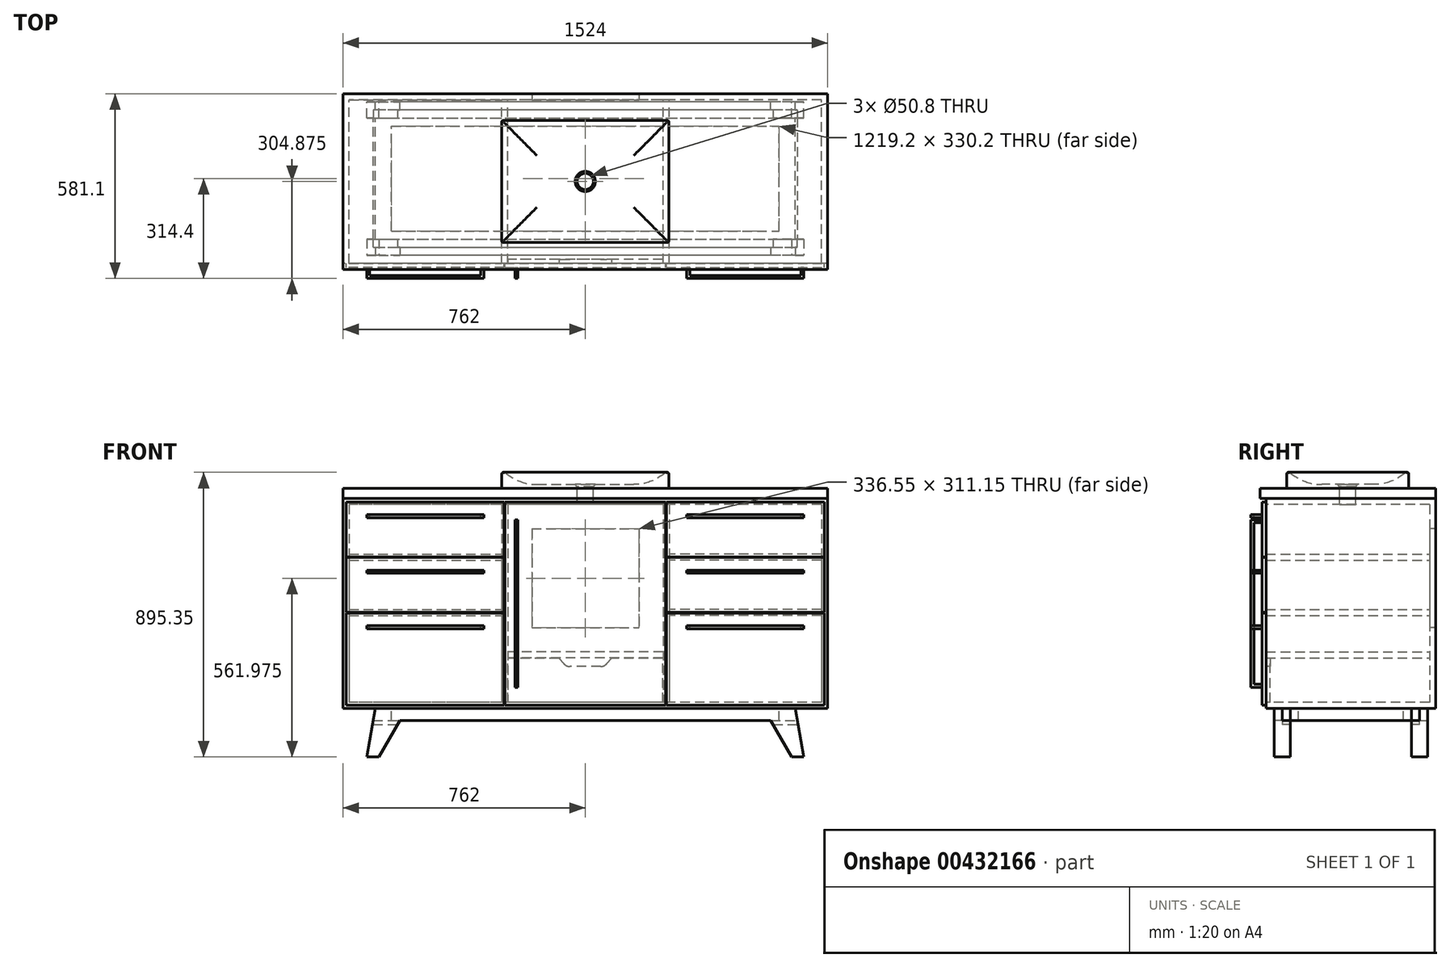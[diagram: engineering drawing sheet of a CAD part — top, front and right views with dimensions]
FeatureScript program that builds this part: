
annotation { "Feature Type Name" : "Feature", "Feature Type Description" : "" }
export const myFeature = defineFeature(function(context is Context, id is Id, definition is map)
    precondition{}
    {
        {
            var Q0;
            Q0=qCreatedBy(makeId("Front.planeOp"),FACE);
            var sketch = newSketch(context, id + "F0", { "sketchPlane" : qUnion([Q0])});
            skLineSegment(sketch, "E0.bottom", {"start": v(762, 330.2) * mm, "end": v(-762, 330.2) * mm});
            skLineSegment(sketch, "E0.top", {"start": v(762, -330.2) * mm, "end": v(-762, -330.2) * mm});
            skLineSegment(sketch, "E0.left", {"start": v(762, 330.2) * mm, "end": v(762, -330.2) * mm});
            skLineSegment(sketch, "E0.right", {"start": v(-762, 330.2) * mm, "end": v(-762, -330.2) * mm});
            skPoint(sketch, "E0.middle", {"position": v(0, 0) * mm});
            skSolve(sketch);
        }
        {
            var Q0;
            Q0=makeQuery(id+"F0.imprint","IMPRINT",FACE,{"disambiguationData":[TD([[makeQuery(id+"F0.imprint","IMPRINT",EDGE,{"derivedFrom":sQuery(id+"F0.wireOp",EDGE,"E0.bottom")}),1.0]])]});
            extrude(context, id + "F1", {"entities" : qUnion([Q0]), "oppositeDirection" : true, "depth" : 533.4 * mm});
        }
        {
            var Q0;
            Q0=makeQuery(id+"F1.opExtrude","CAP_FACE",FACE,{"disambiguationData":[OSD([sQuery(id+"F0.wireOp",EDGE,"E0.bottom"),sQuery(id+"F0.wireOp",EDGE,"E0.top"),sQuery(id+"F0.wireOp",EDGE,"E0.left"),sQuery(id+"F0.wireOp",EDGE,"E0.right")])],"isStart":true});
            var sketch = newSketch(context, id + "F2", { "sketchPlane" : qUnion([Q0])});
            skLineSegment(sketch, "E1.bottom", {"start": v(742.95, 311.15) * mm, "end": v(-742.95, 311.15) * mm});
            skLineSegment(sketch, "E1.top", {"start": v(742.95, -311.15) * mm, "end": v(-742.95, -311.15) * mm});
            skLineSegment(sketch, "E1.left", {"start": v(742.95, 311.15) * mm, "end": v(742.95, -311.15) * mm});
            skLineSegment(sketch, "E1.right", {"start": v(-742.95, 311.15) * mm, "end": v(-742.95, -311.15) * mm});
            skPoint(sketch, "E1.middle", {"position": v(0, 0) * mm});
            skSolve(sketch);
        }
        {
            var Q0;
            Q0=makeQuery(id+"F2.imprint","IMPRINT",FACE,{"disambiguationData":[TD([[makeQuery(id+"F2.imprint","IMPRINT",EDGE,{"derivedFrom":sQuery(id+"F2.wireOp",EDGE,"E1.bottom")}),1.0]])]});
            extrude(context, id + "F3", {"entities" : qUnion([Q0]), "operationType" : NewBodyOperationType.REMOVE, "oppositeDirection" : true, "depth" : 514.35 * mm});
        }
        {
            var Q0;
            Q0=makeQuery(id+"F3.boolean.opBoolean","COPY",FACE,{"derivedFrom":makeQuery(id+"F3.opExtrude","CAP_FACE",FACE,{"disambiguationData":[OSD([sQuery(id+"F2.wireOp",EDGE,"E1.bottom"),sQuery(id+"F2.wireOp",EDGE,"E1.top"),sQuery(id+"F2.wireOp",EDGE,"E1.left"),sQuery(id+"F2.wireOp",EDGE,"E1.right")])],"isStart":false})});
            var sketch = newSketch(context, id + "F4", { "sketchPlane" : qUnion([Q0])});
            skLineSegment(sketch, "E2.bottom", {"start": v(-263.52, 311.15) * mm, "end": v(-244.47, 311.15) * mm});
            skLineSegment(sketch, "E2.top", {"start": v(-263.52, -311.15) * mm, "end": v(-244.47, -311.15) * mm});
            skLineSegment(sketch, "E2.left", {"start": v(-263.53, 311.15) * mm, "end": v(-263.53, -311.15) * mm});
            skLineSegment(sketch, "E2.right", {"start": v(-244.47, 311.15) * mm, "end": v(-244.47, -311.15) * mm});
            skPoint(sketch, "E2.middle", {"position": v(-254, 0) * mm});
            skLineSegment(sketch, "E3.bottom", {"start": v(244.47, 311.15) * mm, "end": v(263.52, 311.15) * mm});
            skLineSegment(sketch, "E3.top", {"start": v(244.47, -311.15) * mm, "end": v(263.52, -311.15) * mm});
            skLineSegment(sketch, "E3.left", {"start": v(244.47, 311.15) * mm, "end": v(244.47, -311.15) * mm});
            skLineSegment(sketch, "E3.right", {"start": v(263.53, 311.15) * mm, "end": v(263.53, -311.15) * mm});
            skPoint(sketch, "E3.middle", {"position": v(254, 0) * mm});
            skLineSegment(sketch, "E4", {"start": v(-742.95, 0) * mm, "end": v(742.95, 0) * mm, "construction": true});
            skSolve(sketch);
        }
        {
            var Q0;
            Q0=makeQuery(id+"F4.imprint","IMPRINT",FACE,{"disambiguationData":[TD([[makeQuery(id+"F4.imprint","IMPRINT",EDGE,{"derivedFrom":sQuery(id+"F4.wireOp",EDGE,"E2.bottom")}),1.0]])]});
            var Q1;
            Q1=makeQuery(id+"F4.imprint","IMPRINT",FACE,{"disambiguationData":[TD([[makeQuery(id+"F4.imprint","IMPRINT",EDGE,{"derivedFrom":sQuery(id+"F4.wireOp",EDGE,"E3.bottom")}),1.0]])]});
            var Q2;
            Q2=makeQuery(id+"F1.opExtrude","CAP_FACE",FACE,{"disambiguationData":[OSD([sQuery(id+"F0.wireOp",EDGE,"E0.bottom"),sQuery(id+"F0.wireOp",EDGE,"E0.top"),sQuery(id+"F0.wireOp",EDGE,"E0.left"),sQuery(id+"F0.wireOp",EDGE,"E0.right")])],"isStart":true});
            extrude(context, id + "F5", {"entities" : qUnion([Q0, Q1]), "endBound" : BoundingType.UP_TO_SURFACE, "endBoundEntityFace" : qUnion([Q2]), "depth" : ((2 * 12) - .75 - .75) * mm});
        }
        {
            var Q0;
            Q0=makeQuery(id+"F3.boolean.opBoolean","COPY",FACE,{"derivedFrom":makeQuery(id+"F3.opExtrude","CAP_FACE",FACE,{"disambiguationData":[OSD([sQuery(id+"F2.wireOp",EDGE,"E1.bottom"),sQuery(id+"F2.wireOp",EDGE,"E1.top"),sQuery(id+"F2.wireOp",EDGE,"E1.left"),sQuery(id+"F2.wireOp",EDGE,"E1.right")])],"isStart":false})});
            var sketch = newSketch(context, id + "F6", { "sketchPlane" : qUnion([Q0])});
            skLineSegment(sketch, "E5", {"start": v(-742.95, 311.15) * mm, "end": v(-263.53, 311.15) * mm, "construction": true});
            skLineSegment(sketch, "E6.bottom", {"start": v(-742.95, 155.58) * mm, "end": v(-263.53, 155.58) * mm});
            skLineSegment(sketch, "E6.top", {"start": v(-742.95, 136.53) * mm, "end": v(-263.53, 136.53) * mm});
            skLineSegment(sketch, "E6.left", {"start": v(-742.95, 155.58) * mm, "end": v(-742.95, 136.53) * mm});
            skLineSegment(sketch, "E6.right", {"start": v(-263.53, 155.58) * mm, "end": v(-263.53, 136.53) * mm});
            skPoint(sketch, "E6.middle", {"position": v(-503.24, 146.05) * mm});
            skPoint(sketch, "E6.middle.positionSnap0", {"position": v(-503.24, 311.15) * mm});
            skPoint(sketch, "E6.centerSnap0", {"position": v(-503.24, 311.15) * mm});
            skLineSegment(sketch, "E7.bottom", {"start": v(-742.95, -19.05) * mm, "end": v(-263.53, -19.05) * mm});
            skLineSegment(sketch, "E7.top", {"start": v(-742.95, -38.1) * mm, "end": v(-263.53, -38.1) * mm});
            skLineSegment(sketch, "E7.left", {"start": v(-742.95, -19.05) * mm, "end": v(-742.95, -38.1) * mm});
            skLineSegment(sketch, "E7.right", {"start": v(-263.53, -19.05) * mm, "end": v(-263.53, -38.1) * mm});
            skPoint(sketch, "E7.middle", {"position": v(-503.24, -28.57) * mm});
            skLineSegment(sketch, "E8", {"start": v(0, 311.15) * mm, "end": v(0, -311.15) * mm, "construction": true});
            skLineSegment(sketch, "E9.MirrorCS", {"start": v(263.53, -19.05) * mm, "end": v(263.53, -38.1) * mm});
            skLineSegment(sketch, "E10.MirrorCS", {"start": v(742.95, -19.05) * mm, "end": v(742.95, -38.1) * mm});
            skLineSegment(sketch, "E11.MirrorCS", {"start": v(742.95, 155.58) * mm, "end": v(742.95, 136.53) * mm});
            skLineSegment(sketch, "E12.MirrorCS", {"start": v(263.53, 155.58) * mm, "end": v(263.53, 136.53) * mm});
            skPoint(sketch, "E13.MirrorP", {"position": v(503.24, 311.15) * mm});
            skLineSegment(sketch, "E14.MirrorCS", {"start": v(742.95, 155.58) * mm, "end": v(263.53, 155.57) * mm});
            skPoint(sketch, "E15.MirrorP", {"position": v(503.24, -28.57) * mm});
            skLineSegment(sketch, "E16.MirrorCS", {"start": v(742.95, -38.1) * mm, "end": v(263.53, -38.1) * mm});
            skLineSegment(sketch, "E17.MirrorCS", {"start": v(742.95, -19.05) * mm, "end": v(263.53, -19.05) * mm});
            skLineSegment(sketch, "E18.MirrorCS", {"start": v(742.95, 136.53) * mm, "end": v(263.53, 136.53) * mm});
            skLineSegment(sketch, "E19.MirrorCS", {"start": v(742.95, 311.15) * mm, "end": v(263.53, 311.15) * mm, "construction": true});
            skPoint(sketch, "E20.MirrorP", {"position": v(503.24, 146.05) * mm});
            skPoint(sketch, "E21.cornerSnap0", {"position": v(-503.24, -19.05) * mm});
            skPoint(sketch, "E22.middle", {"position": v(0, 146.05) * mm});
            skLineSegment(sketch, "E23.bottom", {"start": v(244.47, -152.4) * mm, "end": v(-244.47, -152.4) * mm});
            skLineSegment(sketch, "E23.top", {"start": v(244.47, -171.45) * mm, "end": v(-244.47, -171.45) * mm});
            skLineSegment(sketch, "E23.left", {"start": v(244.47, -152.4) * mm, "end": v(244.47, -171.45) * mm});
            skLineSegment(sketch, "E23.right", {"start": v(-244.47, -152.4) * mm, "end": v(-244.47, -171.45) * mm});
            skPoint(sketch, "E23.middle", {"position": v(0, -161.93) * mm});
            skSolve(sketch);
        }
        {
            var Q0;
            Q0=makeQuery(id+"F6.imprint","IMPRINT",FACE,{"disambiguationData":[TD([[makeQuery(id+"F6.imprint","IMPRINT",EDGE,{"derivedFrom":sQuery(id+"F6.wireOp",EDGE,"E6.bottom")}),-1.0]])]});
            var Q1;
            Q1=makeQuery(id+"F6.imprint","IMPRINT",FACE,{"disambiguationData":[TD([[makeQuery(id+"F6.imprint","IMPRINT",EDGE,{"derivedFrom":sQuery(id+"F6.wireOp",EDGE,"E7.bottom")}),-1.0]])]});
            var Q2;
            Q2=makeQuery(id+"F6.imprint","IMPRINT",FACE,{"disambiguationData":[TD([[makeQuery(id+"F6.imprint","IMPRINT",EDGE,{"derivedFrom":sQuery(id+"F6.wireOp",EDGE,"E11.MirrorCS")}),-1.0]])]});
            var Q3;
            Q3=makeQuery(id+"F6.imprint","IMPRINT",FACE,{"disambiguationData":[TD([[makeQuery(id+"F6.imprint","IMPRINT",EDGE,{"derivedFrom":sQuery(id+"F6.wireOp",EDGE,"E9.MirrorCS")}),1.0]])]});
            var Q4;
            Q4=makeQuery(id+"F1.opExtrude","CAP_FACE",FACE,{"disambiguationData":[OSD([sQuery(id+"F0.wireOp",EDGE,"E0.bottom"),sQuery(id+"F0.wireOp",EDGE,"E0.top"),sQuery(id+"F0.wireOp",EDGE,"E0.left"),sQuery(id+"F0.wireOp",EDGE,"E0.right")])],"isStart":true});
            extrude(context, id + "F7", {"entities" : qUnion([Q0, Q1, Q2, Q3]), "endBound" : BoundingType.UP_TO_SURFACE, "endBoundEntityFace" : qUnion([Q4]), "depth" : 571.5 * mm});
        }
        {
            var Q0;
            Q0=makeQuery(id+"F7.opExtrude","CAP_FACE",FACE,{"disambiguationData":[OSD([sQuery(id+"F6.wireOp",EDGE,"E7.bottom"),sQuery(id+"F6.wireOp",EDGE,"E7.top"),sQuery(id+"F6.wireOp",EDGE,"E7.left"),sQuery(id+"F6.wireOp",EDGE,"E7.right")])],"isStart":false});
            var sketch = newSketch(context, id + "F8", { "sketchPlane" : qUnion([Q0])});
            skLineSegment(sketch, "E24.bottom", {"start": v(-742.95, -38.1) * mm, "end": v(-263.53, -38.1) * mm, "construction": true});
            skLineSegment(sketch, "E24.top", {"start": v(-742.95, -311.15) * mm, "end": v(-263.53, -311.15) * mm, "construction": true});
            skLineSegment(sketch, "E24.left", {"start": v(-742.95, -38.1) * mm, "end": v(-742.95, -311.15) * mm, "construction": true});
            skLineSegment(sketch, "E24.right", {"start": v(-263.52, -38.1) * mm, "end": v(-263.52, -311.15) * mm, "construction": true});
            skLineSegment(sketch, "E25.bottom", {"start": v(-742.95, -19.05) * mm, "end": v(-263.53, -19.05) * mm, "construction": true});
            skLineSegment(sketch, "E25.top", {"start": v(-742.95, 136.53) * mm, "end": v(-263.53, 136.53) * mm, "construction": true});
            skLineSegment(sketch, "E25.left", {"start": v(-742.95, -19.05) * mm, "end": v(-742.95, 136.53) * mm, "construction": true});
            skLineSegment(sketch, "E25.right", {"start": v(-263.53, -19.05) * mm, "end": v(-263.53, 136.53) * mm, "construction": true});
            skLineSegment(sketch, "E26.bottom", {"start": v(-742.95, 311.15) * mm, "end": v(-263.52, 311.15) * mm, "construction": true});
            skLineSegment(sketch, "E26.top", {"start": v(-742.95, 155.58) * mm, "end": v(-263.53, 155.58) * mm, "construction": true});
            skLineSegment(sketch, "E26.left", {"start": v(-742.95, 311.15) * mm, "end": v(-742.95, 155.58) * mm, "construction": true});
            skLineSegment(sketch, "E26.right", {"start": v(-263.52, 311.15) * mm, "end": v(-263.52, 155.58) * mm, "construction": true});
            skLineSegment(sketch, "E27", {"start": v(0, 311.15) * mm, "end": v(0, -311.15) * mm, "construction": true});
            skLineSegment(sketch, "E28.bottom", {"start": v(-254.8, 146.84) * mm, "end": v(-751.68, 146.84) * mm});
            skLineSegment(sketch, "E28.top", {"start": v(-254.8, 319.88) * mm, "end": v(-751.68, 319.88) * mm});
            skLineSegment(sketch, "E28.left", {"start": v(-254.8, 146.84) * mm, "end": v(-254.8, 319.88) * mm});
            skLineSegment(sketch, "E28.right", {"start": v(-751.68, 146.84) * mm, "end": v(-751.68, 319.88) * mm});
            skPoint(sketch, "E28.middle", {"position": v(-503.24, 233.36) * mm});
            skPoint(sketch, "E28.middle.positionSnap0", {"position": v(-503.24, 311.15) * mm});
            skPoint(sketch, "E28.middle.positionSnap1", {"position": v(-742.95, 233.36) * mm});
            skPoint(sketch, "E28.centerSnap0", {"position": v(-503.24, 311.15) * mm});
            skPoint(sketch, "E28.centerSnap1", {"position": v(-742.95, 233.36) * mm});
            skPoint(sketch, "E29.middle.positionSnap0", {"position": v(-503.24, 136.52) * mm});
            skPoint(sketch, "E29.middle.positionSnap1", {"position": v(-742.95, 58.74) * mm});
            skPoint(sketch, "E29.centerSnap0", {"position": v(-503.24, 136.52) * mm});
            skPoint(sketch, "E29.centerSnap1", {"position": v(-742.95, 58.74) * mm});
            skLineSegment(sketch, "E30.bottom", {"start": v(-254.8, -29.37) * mm, "end": v(-751.68, -29.37) * mm});
            skLineSegment(sketch, "E30.top", {"start": v(-254.8, -319.88) * mm, "end": v(-751.68, -319.88) * mm});
            skLineSegment(sketch, "E30.left", {"start": v(-254.8, -29.37) * mm, "end": v(-254.8, -319.88) * mm});
            skLineSegment(sketch, "E30.right", {"start": v(-751.68, -29.37) * mm, "end": v(-751.68, -319.88) * mm});
            skPoint(sketch, "E30.middle", {"position": v(-503.24, -174.63) * mm});
            skPoint(sketch, "E30.middle.positionSnap0", {"position": v(-742.95, -174.63) * mm});
            skPoint(sketch, "E30.middle.positionSnap1", {"position": v(-503.24, -38.1) * mm});
            skPoint(sketch, "E30.centerSnap0", {"position": v(-742.95, -174.63) * mm});
            skPoint(sketch, "E30.centerSnap1", {"position": v(-503.24, -38.1) * mm});
            skLineSegment(sketch, "E31.bottom", {"start": v(-751.68, 145.26) * mm, "end": v(-254.8, 145.26) * mm});
            skLineSegment(sketch, "E31.top", {"start": v(-751.68, -27.78) * mm, "end": v(-254.8, -27.78) * mm});
            skLineSegment(sketch, "E31.left", {"start": v(-751.68, 145.26) * mm, "end": v(-751.68, -27.78) * mm});
            skLineSegment(sketch, "E31.right", {"start": v(-254.8, 145.26) * mm, "end": v(-254.8, -27.78) * mm});
            skPoint(sketch, "E31.middle", {"position": v(-503.24, 58.74) * mm});
            skLineSegment(sketch, "E32.MirrorCS", {"start": v(751.68, 146.84) * mm, "end": v(751.68, 319.88) * mm});
            skLineSegment(sketch, "E33.MirrorCS", {"start": v(751.68, 145.26) * mm, "end": v(751.68, -27.78) * mm});
            skLineSegment(sketch, "E34.MirrorCS", {"start": v(254.8, -319.88) * mm, "end": v(751.68, -319.88) * mm});
            skPoint(sketch, "E35.MirrorP", {"position": v(742.95, -174.62) * mm});
            skLineSegment(sketch, "E36.MirrorCS", {"start": v(751.68, -27.78) * mm, "end": v(254.8, -27.78) * mm});
            skLineSegment(sketch, "E37.MirrorCS", {"start": v(254.8, 146.84) * mm, "end": v(751.68, 146.84) * mm});
            skLineSegment(sketch, "E38.MirrorCS", {"start": v(254.8, -29.37) * mm, "end": v(254.8, -319.88) * mm});
            skPoint(sketch, "E39.MirrorP", {"position": v(503.24, 311.15) * mm});
            skPoint(sketch, "E40.MirrorP", {"position": v(503.24, -38.1) * mm});
            skLineSegment(sketch, "E41.MirrorCS", {"start": v(254.8, 319.88) * mm, "end": v(751.68, 319.88) * mm});
            skLineSegment(sketch, "E42.MirrorCS", {"start": v(751.68, 145.26) * mm, "end": v(254.8, 145.26) * mm});
            skPoint(sketch, "E43.MirrorP", {"position": v(742.95, 233.36) * mm});
            skLineSegment(sketch, "E44.MirrorCS", {"start": v(254.8, 146.84) * mm, "end": v(254.8, 319.88) * mm});
            skLineSegment(sketch, "E45.MirrorCS", {"start": v(751.68, -29.37) * mm, "end": v(751.68, -319.88) * mm});
            skPoint(sketch, "E46.MirrorP", {"position": v(503.24, 136.53) * mm});
            skLineSegment(sketch, "E47.MirrorCS", {"start": v(254.8, 145.26) * mm, "end": v(254.8, -27.78) * mm});
            skPoint(sketch, "E48.MirrorP", {"position": v(742.95, 58.74) * mm});
            skPoint(sketch, "E49.MirrorP", {"position": v(503.24, 233.36) * mm});
            skLineSegment(sketch, "E50.MirrorCS", {"start": v(742.95, -311.15) * mm, "end": v(263.53, -311.15) * mm, "construction": true});
            skLineSegment(sketch, "E51.MirrorCS", {"start": v(742.95, -19.05) * mm, "end": v(742.95, 136.53) * mm, "construction": true});
            skLineSegment(sketch, "E52.MirrorCS", {"start": v(742.95, -38.1) * mm, "end": v(742.95, -311.15) * mm, "construction": true});
            skPoint(sketch, "E53.MirrorP", {"position": v(503.24, 58.74) * mm});
            skLineSegment(sketch, "E54.MirrorCS", {"start": v(263.52, -38.1) * mm, "end": v(263.52, -311.15) * mm, "construction": true});
            skLineSegment(sketch, "E55.MirrorCS", {"start": v(742.95, -19.05) * mm, "end": v(263.53, -19.05) * mm, "construction": true});
            skLineSegment(sketch, "E56.MirrorCS", {"start": v(263.52, 311.15) * mm, "end": v(263.52, 155.58) * mm, "construction": true});
            skLineSegment(sketch, "E57.MirrorCS", {"start": v(742.95, 311.15) * mm, "end": v(742.95, 155.58) * mm, "construction": true});
            skLineSegment(sketch, "E58.MirrorCS", {"start": v(742.95, -38.1) * mm, "end": v(263.53, -38.1) * mm, "construction": true});
            skLineSegment(sketch, "E59.MirrorCS", {"start": v(742.95, 155.58) * mm, "end": v(263.52, 155.58) * mm, "construction": true});
            skLineSegment(sketch, "E60.MirrorCS", {"start": v(742.95, 136.53) * mm, "end": v(263.53, 136.53) * mm, "construction": true});
            skPoint(sketch, "E61.MirrorP", {"position": v(503.24, -174.62) * mm});
            skLineSegment(sketch, "E62.MirrorCS", {"start": v(263.53, -19.05) * mm, "end": v(263.53, 136.53) * mm, "construction": true});
            skLineSegment(sketch, "E63.MirrorCS", {"start": v(254.8, -29.37) * mm, "end": v(751.68, -29.37) * mm});
            skLineSegment(sketch, "E64.MirrorCS", {"start": v(742.95, 311.15) * mm, "end": v(263.52, 311.15) * mm, "construction": true});
            skSolve(sketch);
        }
        {
            var Q0;
            Q0=makeQuery(id+"F8.imprint","IMPRINT",FACE,{"disambiguationData":[TD([[makeQuery(id+"F8.imprint","IMPRINT",EDGE,{"derivedFrom":sQuery(id+"F8.wireOp",EDGE,"E28.bottom")}),-1.0]])]});
            var Q1;
            Q1=makeQuery(id+"F8.imprint","IMPRINT",FACE,{"disambiguationData":[TD([[makeQuery(id+"F8.imprint","IMPRINT",EDGE,{"derivedFrom":sQuery(id+"F8.wireOp",EDGE,"E31.bottom")}),-1.0]])]});
            var Q2;
            Q2=makeQuery(id+"F8.imprint","IMPRINT",FACE,{"disambiguationData":[TD([[makeQuery(id+"F8.imprint","IMPRINT",EDGE,{"derivedFrom":sQuery(id+"F8.wireOp",EDGE,"E32.MirrorCS")}),1.0]])]});
            var Q3;
            Q3=makeQuery(id+"F8.imprint","IMPRINT",FACE,{"disambiguationData":[TD([[makeQuery(id+"F8.imprint","IMPRINT",EDGE,{"derivedFrom":sQuery(id+"F8.wireOp",EDGE,"E33.MirrorCS")}),-1.0]])]});
            var Q4;
            Q4=makeQuery(id+"F8.imprint","IMPRINT",FACE,{"disambiguationData":[TD([[makeQuery(id+"F8.imprint","IMPRINT",EDGE,{"derivedFrom":sQuery(id+"F8.wireOp",EDGE,"E34.MirrorCS")}),1.0]])]});
            var Q5;
            {var subQ5=makeQuery(id+"F7.opExtrude","CAP_EDGE",EDGE,{"disambiguationData":[OSD([sQuery(id+"F6.wireOp",EDGE,"E7.top")])],"isStart":false});Q5=makeQuery(id+"F8.imprint","IMPRINT",FACE,{"disambiguationData":[TD([[makeQuery(id+"F8.imprint","IMPRINT",EDGE,{"derivedFrom":subQ5}),1.0]])]});}
            var Q6;
            Q6=makeQuery(id+"F8.imprint","IMPRINT",FACE,{"disambiguationData":[TD([[makeQuery(id+"F8.imprint","IMPRINT",EDGE,{"derivedFrom":sQuery(id+"F8.wireOp",EDGE,"E30.top")}),-1.0]])]});
            var Q7;
            {var subQ5=makeQuery(id+"F7.opExtrude","CAP_EDGE",EDGE,{"disambiguationData":[OSD([sQuery(id+"F6.wireOp",EDGE,"E7.bottom")])],"isStart":false});Q7=makeQuery(id+"F8.imprint","IMPRINT",FACE,{"disambiguationData":[TD([[makeQuery(id+"F8.imprint","IMPRINT",EDGE,{"derivedFrom":subQ5}),-1.0]])]});}
            extrude(context, id + "F9", {"entities" : qUnion([Q0, Q1, Q2, Q3, Q4, Q5, Q6, Q7]), "depth" : 12.7 * mm});
        }
        {
            var Q0;
            Q0=qCreatedBy(makeId("Front.planeOp"),FACE);
            var sketch = newSketch(context, id + "F10", { "sketchPlane" : qUnion([Q0])});
            skLineSegment(sketch, "E65.bottom", {"start": v(-253.2, -319.88) * mm, "end": v(253.2, -319.88) * mm});
            skLineSegment(sketch, "E65.top", {"start": v(-253.2, 319.88) * mm, "end": v(253.2, 319.88) * mm});
            skLineSegment(sketch, "E65.left", {"start": v(-253.2, -319.88) * mm, "end": v(-253.2, 319.88) * mm});
            skLineSegment(sketch, "E65.right", {"start": v(253.2, -319.88) * mm, "end": v(253.2, 319.88) * mm});
            skPoint(sketch, "E65.middle", {"position": v(0, 0) * mm});
            skSolve(sketch);
        }
        {
            var Q0;
            Q0=makeQuery(id+"F10.imprint","IMPRINT",FACE,{"disambiguationData":[TD([[makeQuery(id+"F10.imprint","IMPRINT",EDGE,{"derivedFrom":sQuery(id+"F10.wireOp",EDGE,"E65.bottom")}),1.0]])]});
            extrude(context, id + "F11", {"entities" : qUnion([Q0]), "depth" : 12.7 * mm});
        }
        {
            var Q0;
            Q0=makeQuery(id+"F6.imprint","IMPRINT",FACE,{"disambiguationData":[TD([[makeQuery(id+"F6.imprint","IMPRINT",EDGE,{"derivedFrom":sQuery(id+"F6.wireOp",EDGE,"E23.bottom")}),1.0]])]});
            var Q1;
            Q1=makeQuery(id+"F1.opExtrude","CAP_FACE",FACE,{"disambiguationData":[OSD([sQuery(id+"F0.wireOp",EDGE,"E0.bottom"),sQuery(id+"F0.wireOp",EDGE,"E0.top"),sQuery(id+"F0.wireOp",EDGE,"E0.left"),sQuery(id+"F0.wireOp",EDGE,"E0.right")])],"isStart":true});
            extrude(context, id + "F12", {"entities" : qUnion([Q0]), "endBound" : BoundingType.UP_TO_SURFACE, "endBoundEntityFace" : qUnion([Q1]), "depth" : 533.4 * mm});
        }
        {
            var Q0;
            Q0=makeQuery(id+"F1.opExtrude","SWEPT_FACE",FACE,{"disambiguationData":[OSD([sQuery(id+"F0.wireOp",EDGE,"E0.top")])]});
            var sketch = newSketch(context, id + "F13", { "sketchPlane" : qUnion([Q0])});
            skLineSegment(sketch, "E66.bottom", {"start": v(660.4, -50.8) * mm, "end": v(-660.4, -50.8) * mm});
            skLineSegment(sketch, "E66.top", {"start": v(660.4, -482.6) * mm, "end": v(-660.4, -482.6) * mm});
            skLineSegment(sketch, "E66.left", {"start": v(660.4, -50.8) * mm, "end": v(660.4, -482.6) * mm});
            skLineSegment(sketch, "E66.right", {"start": v(-660.4, -50.8) * mm, "end": v(-660.4, -482.6) * mm});
            skPoint(sketch, "E66.middle", {"position": v(0, -266.7) * mm});
            skPoint(sketch, "E66.middle.positionSnap0", {"position": v(-762, -266.7) * mm});
            skPoint(sketch, "E66.centerSnap0", {"position": v(-762, -266.7) * mm});
            skLineSegment(sketch, "E67.bottom", {"start": v(-609.6, -101.6) * mm, "end": v(609.6, -101.6) * mm});
            skLineSegment(sketch, "E67.top", {"start": v(-609.6, -431.8) * mm, "end": v(609.6, -431.8) * mm});
            skLineSegment(sketch, "E67.left", {"start": v(-609.6, -101.6) * mm, "end": v(-609.6, -431.8) * mm});
            skLineSegment(sketch, "E67.right", {"start": v(609.6, -101.6) * mm, "end": v(609.6, -431.8) * mm});
            skSolve(sketch);
        }
        {
            var Q0;
            Q0=makeQuery(id+"F13.imprint","IMPRINT",FACE,{"disambiguationData":[TD([[makeQuery(id+"F13.imprint","IMPRINT",EDGE,{"derivedFrom":sQuery(id+"F13.wireOp",EDGE,"E66.bottom")}),1.0]])]});
            extrude(context, id + "F14", {"entities" : qUnion([Q0]), "depth" : 38.1 * mm});
        }
        {
            var Q0;
            Q0=makeQuery(id+"F14.opExtrude","SWEPT_FACE",FACE,{"disambiguationData":[OSD([sQuery(id+"F13.wireOp",EDGE,"E66.bottom")])]});
            var sketch = newSketch(context, id + "F15", { "sketchPlane" : qUnion([Q0])});
            skLineSegment(sketch, "E68", {"start": v(-660.4, -330.2) * mm, "end": v(-687.27, -482.6) * mm});
            skLineSegment(sketch, "E69", {"start": v(-687.27, -482.6) * mm, "end": v(-649.17, -482.6) * mm});
            skLineSegment(sketch, "E70", {"start": v(-649.17, -482.6) * mm, "end": v(-583.18, -368.3) * mm});
            skLineSegment(sketch, "E71", {"start": v(0, -330.2) * mm, "end": v(0, -368.3) * mm, "construction": true});
            skLineSegment(sketch, "E72.MirrorCS", {"start": v(687.27, -482.6) * mm, "end": v(649.17, -482.6) * mm});
            skLineSegment(sketch, "E73.MirrorCS", {"start": v(660.4, -330.2) * mm, "end": v(687.27, -482.6) * mm});
            skLineSegment(sketch, "E74.MirrorCS", {"start": v(649.17, -482.6) * mm, "end": v(583.18, -368.3) * mm});
            skLineSegment(sketch, "E75", {"start": v(-583.18, -368.3) * mm, "end": v(583.18, -368.3) * mm});
            skLineSegment(sketch, "E76", {"start": v(-660.4, -330.2) * mm, "end": v(660.4, -330.2) * mm});
            skSolve(sketch);
        }
        {
            var Q0;
            Q0=makeQuery(id+"F10.imprint","IMPRINT",FACE,{"disambiguationData":[TD([[makeQuery(id+"F10.imprint","IMPRINT",EDGE,{"derivedFrom":sQuery(id+"F10.wireOp",EDGE,"E65.bottom")}),1.0]])]});
            cPlane(context, id + "F16", {"entities" : qUnion([Q0]), "cplaneType" : CPlaneType.OFFSET, "offset" : 266.7 * mm, "oppositeDirection" : true, "width" : 152.4 * mm, "height" : 152.4 * mm});
        }
        {
            var Q0;
            Q0=qSketchRegion(id+"F15",true);
            extrude(context, id + "F17", {"entities" : qUnion([Q0]), "oppositeDirection" : true, "depth" : 25.4 * mm, "hasSecondDirection" : true, "secondDirectionOppositeDirection" : false, "secondDirectionDepth" : 25.4 * mm});
        }
        {
            var Q0;
            Q0=makeQuery(id+"F17.opExtrude","SWEPT_BODY",BODY,{"disambiguationData":[OSD([sQuery(id+"F15.wireOp",EDGE,"E68"),sQuery(id+"F15.wireOp",EDGE,"E69"),sQuery(id+"F15.wireOp",EDGE,"E70"),sQuery(id+"F15.wireOp",EDGE,"E72.MirrorCS"),sQuery(id+"F15.wireOp",EDGE,"E73.MirrorCS"),sQuery(id+"F15.wireOp",EDGE,"E74.MirrorCS"),sQuery(id+"F15.wireOp",EDGE,"E75"),sQuery(id+"F15.wireOp",EDGE,"E76")])]});
            var Q1;
            Q1=qCreatedBy(id+"F16.planeOp",FACE);
            mirror(context, id + "F18", {"entities" : qUnion([Q0]), "mirrorPlane" : qUnion([Q1])});
        }
        {
            var Q0;
            Q0=makeQuery(id+"F1.opExtrude","SWEPT_FACE",FACE,{"disambiguationData":[OSD([sQuery(id+"F0.wireOp",EDGE,"E0.bottom")])]});
            var sketch = newSketch(context, id + "F19", { "sketchPlane" : qUnion([Q0])});
            skLineSegment(sketch, "E77.bottom", {"start": v(-762, 533.4) * mm, "end": v(762, 533.4) * mm});
            skLineSegment(sketch, "E77.top", {"start": v(-762, -19.05) * mm, "end": v(762, -19.05) * mm});
            skLineSegment(sketch, "E77.left", {"start": v(-762, 533.4) * mm, "end": v(-762, -19.05) * mm});
            skLineSegment(sketch, "E77.right", {"start": v(762, 533.4) * mm, "end": v(762, -19.05) * mm});
            skPoint(sketch, "E77.middle.positionSnap0", {"position": v(0, 533.4) * mm});
            skPoint(sketch, "E77.centerSnap0", {"position": v(0, 533.4) * mm});
            skSolve(sketch);
        }
        {
            var Q0;
            Q0=makeQuery(id+"F19.imprint","IMPRINT",FACE,{"disambiguationData":[TD([[makeQuery(id+"F19.imprint","IMPRINT",EDGE,{"derivedFrom":sQuery(id+"F19.wireOp",EDGE,"E77.bottom")}),1.0]])]});
            var Q1;
            {var subQ0=sQuery(id+"F19.wireOp",EDGE,"E77.top");Q1=makeQuery(id+"F19.imprint","IMPRINT",FACE,{"disambiguationData":[TD([[makeQuery(id+"F19.imprint","IMPRINT",EDGE,{"derivedFrom":subQ0}),1.0]])]});}
            extrude(context, id + "F20", {"entities" : qUnion([Q0, Q1]), "depth" : 31.75 * mm});
        }
        {
            var Q0;
            Q0=makeQuery(id+"F11.opExtrude","CAP_FACE",FACE,{"disambiguationData":[OSD([sQuery(id+"F10.wireOp",EDGE,"E65.bottom"),sQuery(id+"F10.wireOp",EDGE,"E65.top"),sQuery(id+"F10.wireOp",EDGE,"E65.left"),sQuery(id+"F10.wireOp",EDGE,"E65.right")])],"isStart":false});
            var sketch = newSketch(context, id + "F21", { "sketchPlane" : qUnion([Q0])});
            skLineSegment(sketch, "E78.bottom", {"start": v(-221.46, -263.5) * mm, "end": v(-211.93, -263.5) * mm});
            skLineSegment(sketch, "E78.top", {"start": v(-221.46, 263.5) * mm, "end": v(-211.93, 263.5) * mm});
            skLineSegment(sketch, "E78.left", {"start": v(-221.46, -263.5) * mm, "end": v(-221.46, 263.5) * mm});
            skLineSegment(sketch, "E78.right", {"start": v(-211.93, -263.5) * mm, "end": v(-211.93, 263.5) * mm});
            skLineSegment(sketch, "E79", {"start": v(0, 0) * mm, "end": v(-211.93, 0) * mm, "construction": true});
            skSolve(sketch);
        }
        {
            var Q0;
            Q0=makeQuery(id+"F21.imprint","IMPRINT",FACE,{"disambiguationData":[TD([[makeQuery(id+"F21.imprint","IMPRINT",EDGE,{"derivedFrom":sQuery(id+"F21.wireOp",EDGE,"E78.bottom")}),1.0]])]});
            extrude(context, id + "F22", {"entities" : qUnion([Q0]), "depth" : 35 * mm});
        }
        {
            var Q0;
            Q0=makeQuery(id+"F22.opExtrude","SWEPT_FACE",FACE,{"disambiguationData":[OSD([sQuery(id+"F21.wireOp",EDGE,"E78.right")])]});
            var sketch = newSketch(context, id + "F23", { "sketchPlane" : qUnion([Q0])});
            skLineSegment(sketch, "E80.bottom", {"start": v(-12.7, -253.97) * mm, "end": v(-38.17, -253.97) * mm});
            skLineSegment(sketch, "E80.top", {"start": v(-12.7, 253.97) * mm, "end": v(-38.18, 253.97) * mm});
            skLineSegment(sketch, "E80.left", {"start": v(-12.7, 253.97) * mm, "end": v(-12.7, -253.98) * mm});
            skLineSegment(sketch, "E80.right", {"start": v(-38.18, 253.97) * mm, "end": v(-38.18, -253.97) * mm});
            skSolve(sketch);
        }
        {
            var Q0;
            Q0=makeQuery(id+"F23.imprint","IMPRINT",FACE,{"disambiguationData":[TD([[makeQuery(id+"F23.imprint","IMPRINT",EDGE,{"derivedFrom":sQuery(id+"F23.wireOp",EDGE,"E80.bottom")}),-1.0]])]});
            extrude(context, id + "F24", {"entities" : qUnion([Q0]), "operationType" : NewBodyOperationType.REMOVE, "oppositeDirection" : true, "depth" : 25.4 * mm});
        }
        {
            var Q0;
            Q0=makeQuery(id+"F9.opExtrude","CAP_FACE",FACE,{"disambiguationData":[OSD([sQuery(id+"F0.wireOp",EDGE,"E0.bottom"),sQuery(id+"F0.wireOp",EDGE,"E0.top"),sQuery(id+"F0.wireOp",EDGE,"E0.left"),sQuery(id+"F0.wireOp",EDGE,"E0.right"),sQuery(id+"F6.wireOp",EDGE,"E7.top"),sQuery(id+"F6.wireOp",EDGE,"E7.left"),sQuery(id+"F6.wireOp",EDGE,"E7.right"),sQuery(id+"F8.wireOp",EDGE,"E30.bottom"),sQuery(id+"F8.wireOp",EDGE,"E30.top"),sQuery(id+"F8.wireOp",EDGE,"E30.left"),sQuery(id+"F8.wireOp",EDGE,"E30.right")])],"isStart":false});
            var sketch = newSketch(context, id + "F25", { "sketchPlane" : qUnion([Q0])});
            skLineSegment(sketch, "E81.bottom", {"start": v(687.24, 269.88) * mm, "end": v(319.24, 269.88) * mm});
            skLineSegment(sketch, "E81.top", {"start": v(687.24, 279.4) * mm, "end": v(319.24, 279.4) * mm});
            skLineSegment(sketch, "E81.left", {"start": v(687.24, 269.88) * mm, "end": v(687.24, 279.4) * mm});
            skLineSegment(sketch, "E81.right", {"start": v(319.24, 269.88) * mm, "end": v(319.24, 279.4) * mm});
            skPoint(sketch, "E81.middle", {"position": v(503.24, 274.64) * mm});
            skPoint(sketch, "E81.middle.positionSnap0", {"position": v(503.24, 319.88) * mm});
            skPoint(sketch, "E81.centerSnap0", {"position": v(503.24, 319.88) * mm});
            skLineSegment(sketch, "E82.bottom", {"start": v(687.24, 104.78) * mm, "end": v(319.24, 104.78) * mm});
            skLineSegment(sketch, "E82.top", {"start": v(687.24, 95.25) * mm, "end": v(319.24, 95.25) * mm});
            skLineSegment(sketch, "E82.left", {"start": v(687.24, 104.78) * mm, "end": v(687.24, 95.25) * mm});
            skLineSegment(sketch, "E82.right", {"start": v(319.24, 104.78) * mm, "end": v(319.24, 95.25) * mm});
            skPoint(sketch, "E82.middle", {"position": v(503.24, 100.01) * mm});
            skLineSegment(sketch, "E83.bottom", {"start": v(687.24, -69.85) * mm, "end": v(319.24, -69.85) * mm});
            skLineSegment(sketch, "E83.top", {"start": v(687.24, -79.37) * mm, "end": v(319.24, -79.37) * mm});
            skLineSegment(sketch, "E83.left", {"start": v(687.24, -69.85) * mm, "end": v(687.24, -79.37) * mm});
            skLineSegment(sketch, "E83.right", {"start": v(319.24, -69.85) * mm, "end": v(319.24, -79.37) * mm});
            skPoint(sketch, "E83.middle", {"position": v(503.24, -74.61) * mm});
            skPoint(sketch, "E83.middle.positionSnap0", {"position": v(503.24, 95.25) * mm});
            skPoint(sketch, "E83.centerSnap0", {"position": v(503.24, 95.25) * mm});
            skLineSegment(sketch, "E84", {"start": v(0, 319.88) * mm, "end": v(0, -311.15) * mm, "construction": true});
            skLineSegment(sketch, "E85.MirrorCS", {"start": v(-687.24, 104.78) * mm, "end": v(-687.24, 95.25) * mm});
            skLineSegment(sketch, "E86.MirrorCS", {"start": v(-319.24, 104.78) * mm, "end": v(-319.24, 95.25) * mm});
            skLineSegment(sketch, "E87.MirrorCS", {"start": v(-319.24, -69.85) * mm, "end": v(-319.24, -79.37) * mm});
            skLineSegment(sketch, "E88.MirrorCS", {"start": v(-687.24, -69.85) * mm, "end": v(-687.24, -79.37) * mm});
            skLineSegment(sketch, "E89.MirrorCS", {"start": v(-687.24, 269.88) * mm, "end": v(-687.24, 279.4) * mm});
            skLineSegment(sketch, "E90.MirrorCS", {"start": v(-319.24, 269.88) * mm, "end": v(-319.24, 279.4) * mm});
            skPoint(sketch, "E91.MirrorP", {"position": v(-503.24, 95.25) * mm});
            skPoint(sketch, "E92.MirrorP", {"position": v(-503.24, 319.88) * mm});
            skPoint(sketch, "E93.MirrorP", {"position": v(-503.24, 100.01) * mm});
            skLineSegment(sketch, "E94.MirrorCS", {"start": v(-687.24, 269.88) * mm, "end": v(-319.24, 269.88) * mm});
            skLineSegment(sketch, "E95.MirrorCS", {"start": v(-687.24, 279.4) * mm, "end": v(-319.24, 279.4) * mm});
            skLineSegment(sketch, "E96.MirrorCS", {"start": v(-687.24, -69.85) * mm, "end": v(-319.24, -69.85) * mm});
            skLineSegment(sketch, "E97.MirrorCS", {"start": v(-687.24, -79.37) * mm, "end": v(-319.24, -79.37) * mm});
            skLineSegment(sketch, "E98.MirrorCS", {"start": v(-687.24, 95.25) * mm, "end": v(-319.24, 95.25) * mm});
            skPoint(sketch, "E99.MirrorP", {"position": v(-503.24, 274.64) * mm});
            skLineSegment(sketch, "E100.MirrorCS", {"start": v(-687.24, 104.78) * mm, "end": v(-319.24, 104.78) * mm});
            skPoint(sketch, "E101.MirrorP", {"position": v(-503.24, -74.61) * mm});
            skSolve(sketch);
        }
        {
            var Q0;
            Q0=makeQuery(id+"F25.imprint","IMPRINT",FACE,{"disambiguationData":[TD([[makeQuery(id+"F25.imprint","IMPRINT",EDGE,{"derivedFrom":sQuery(id+"F25.wireOp",EDGE,"E89.MirrorCS")}),-1.0]])]});
            var Q1;
            Q1=makeQuery(id+"F25.imprint","IMPRINT",FACE,{"disambiguationData":[TD([[makeQuery(id+"F25.imprint","IMPRINT",EDGE,{"derivedFrom":sQuery(id+"F25.wireOp",EDGE,"E85.MirrorCS")}),1.0]])]});
            var Q2;
            Q2=makeQuery(id+"F25.imprint","IMPRINT",FACE,{"disambiguationData":[TD([[makeQuery(id+"F25.imprint","IMPRINT",EDGE,{"derivedFrom":sQuery(id+"F25.wireOp",EDGE,"E87.MirrorCS")}),-1.0]])]});
            var Q3;
            Q3=makeQuery(id+"F25.imprint","IMPRINT",FACE,{"disambiguationData":[TD([[makeQuery(id+"F25.imprint","IMPRINT",EDGE,{"derivedFrom":sQuery(id+"F25.wireOp",EDGE,"E81.bottom")}),-1.0]])]});
            var Q4;
            Q4=makeQuery(id+"F25.imprint","IMPRINT",FACE,{"disambiguationData":[TD([[makeQuery(id+"F25.imprint","IMPRINT",EDGE,{"derivedFrom":sQuery(id+"F25.wireOp",EDGE,"E82.bottom")}),1.0]])]});
            var Q5;
            Q5=makeQuery(id+"F25.imprint","IMPRINT",FACE,{"disambiguationData":[TD([[makeQuery(id+"F25.imprint","IMPRINT",EDGE,{"derivedFrom":sQuery(id+"F25.wireOp",EDGE,"E83.bottom")}),1.0]])]});
            extrude(context, id + "F26", {"entities" : qUnion([Q0, Q1, Q2, Q3, Q4, Q5]), "depth" : 35 * mm});
        }
        {
            var Q0;
            Q0=makeQuery(id+"F26.opExtrude","SWEPT_FACE",FACE,{"disambiguationData":[OSD([sQuery(id+"F25.wireOp",EDGE,"E95.MirrorCS")])]});
            var sketch = newSketch(context, id + "F27", { "sketchPlane" : qUnion([Q0])});
            skLineSegment(sketch, "E102.bottom", {"start": v(-677.71, -12.7) * mm, "end": v(-328.76, -12.7) * mm});
            skLineSegment(sketch, "E102.top", {"start": v(-677.71, -38.18) * mm, "end": v(-328.76, -38.17) * mm});
            skLineSegment(sketch, "E102.left", {"start": v(-677.71, -12.7) * mm, "end": v(-677.71, -38.18) * mm});
            skLineSegment(sketch, "E102.right", {"start": v(-328.76, -12.7) * mm, "end": v(-328.76, -38.17) * mm});
            skSolve(sketch);
        }
        {
            var Q0;
            Q0=makeQuery(id+"F27.imprint","IMPRINT",FACE,{"disambiguationData":[TD([[makeQuery(id+"F27.imprint","IMPRINT",EDGE,{"derivedFrom":sQuery(id+"F27.wireOp",EDGE,"E102.bottom")}),-1.0]])]});
            var Q1;
            Q1=makeQuery(id+"F27.imprint","IMPRINT",FACE,{"disambiguationData":[TD([[makeQuery(id+"F27.imprint","IMPRINT",EDGE,{"derivedFrom":sQuery(id+"F27.wireOp",EDGE,"vdCn5M4T-uzS2-vMqU-omqx-BEMn8WxRvKta.bottom")}),-1.0]])]});
            extrude(context, id + "F28", {"entities" : qUnion([Q0, Q1]), "operationType" : NewBodyOperationType.REMOVE, "endBound" : BoundingType.THROUGH_ALL, "oppositeDirection" : true, "depth" : 25.4 * mm});
        }
        {
            var Q0;
            Q0=makeQuery(id+"F26.opExtrude","SWEPT_FACE",FACE,{"disambiguationData":[OSD([sQuery(id+"F25.wireOp",EDGE,"E100.MirrorCS")])]});
            var sketch = newSketch(context, id + "F29", { "sketchPlane" : qUnion([Q0])});
            skLineSegment(sketch, "E103.bottom", {"start": v(-677.71, -12.7) * mm, "end": v(-328.76, -12.7) * mm});
            skLineSegment(sketch, "E103.top", {"start": v(-677.71, -38.18) * mm, "end": v(-328.76, -38.18) * mm});
            skLineSegment(sketch, "E103.left", {"start": v(-677.71, -12.7) * mm, "end": v(-677.71, -38.18) * mm});
            skLineSegment(sketch, "E103.right", {"start": v(-328.76, -12.7) * mm, "end": v(-328.76, -38.17) * mm});
            skSolve(sketch);
        }
        {
            var Q0;
            Q0=makeQuery(id+"F29.imprint","IMPRINT",FACE,{"disambiguationData":[TD([[makeQuery(id+"F29.imprint","IMPRINT",EDGE,{"derivedFrom":sQuery(id+"F29.wireOp",EDGE,"E103.bottom")}),-1.0]])]});
            extrude(context, id + "F30", {"entities" : qUnion([Q0]), "operationType" : NewBodyOperationType.REMOVE, "oppositeDirection" : true, "depth" : 25.4 * mm});
        }
        {
            var Q0;
            Q0=makeQuery(id+"F26.opExtrude","SWEPT_FACE",FACE,{"disambiguationData":[OSD([sQuery(id+"F25.wireOp",EDGE,"E96.MirrorCS")])]});
            var sketch = newSketch(context, id + "F31", { "sketchPlane" : qUnion([Q0])});
            skLineSegment(sketch, "E104.bottom", {"start": v(-677.71, -12.7) * mm, "end": v(-328.76, -12.7) * mm});
            skLineSegment(sketch, "E104.top", {"start": v(-677.71, -38.18) * mm, "end": v(-328.76, -38.18) * mm});
            skLineSegment(sketch, "E104.left", {"start": v(-677.71, -12.7) * mm, "end": v(-677.71, -38.18) * mm});
            skLineSegment(sketch, "E104.right", {"start": v(-328.76, -12.7) * mm, "end": v(-328.76, -38.17) * mm});
            skSolve(sketch);
        }
        {
            var Q0;
            Q0=makeQuery(id+"F31.imprint","IMPRINT",FACE,{"disambiguationData":[TD([[makeQuery(id+"F31.imprint","IMPRINT",EDGE,{"derivedFrom":sQuery(id+"F31.wireOp",EDGE,"E104.bottom")}),-1.0]])]});
            extrude(context, id + "F32", {"entities" : qUnion([Q0]), "operationType" : NewBodyOperationType.REMOVE, "oppositeDirection" : true, "depth" : 25.4 * mm});
        }
        {
            var Q0;
            Q0=makeQuery(id+"F26.opExtrude","SWEPT_FACE",FACE,{"disambiguationData":[OSD([sQuery(id+"F25.wireOp",EDGE,"E81.top")])]});
            var sketch = newSketch(context, id + "F33", { "sketchPlane" : qUnion([Q0])});
            skLineSegment(sketch, "E105.bottom", {"start": v(328.76, -12.7) * mm, "end": v(677.71, -12.7) * mm});
            skLineSegment(sketch, "E105.top", {"start": v(328.76, -38.18) * mm, "end": v(677.71, -38.17) * mm});
            skLineSegment(sketch, "E105.left", {"start": v(328.76, -12.7) * mm, "end": v(328.76, -38.18) * mm});
            skLineSegment(sketch, "E105.right", {"start": v(677.71, -12.7) * mm, "end": v(677.71, -38.17) * mm});
            skSolve(sketch);
        }
        {
            var Q0;
            Q0=makeQuery(id+"F33.imprint","IMPRINT",FACE,{"disambiguationData":[TD([[makeQuery(id+"F33.imprint","IMPRINT",EDGE,{"derivedFrom":sQuery(id+"F33.wireOp",EDGE,"E105.bottom")}),1.0]])]});
            extrude(context, id + "F34", {"entities" : qUnion([Q0]), "operationType" : NewBodyOperationType.REMOVE, "oppositeDirection" : true, "depth" : 25.4 * mm});
        }
        {
            var Q0;
            Q0=makeQuery(id+"F26.opExtrude","SWEPT_FACE",FACE,{"disambiguationData":[OSD([sQuery(id+"F25.wireOp",EDGE,"E82.bottom")])]});
            var sketch = newSketch(context, id + "F35", { "sketchPlane" : qUnion([Q0])});
            skLineSegment(sketch, "E106.bottom", {"start": v(328.76, -12.7) * mm, "end": v(677.71, -12.7) * mm});
            skLineSegment(sketch, "E106.top", {"start": v(328.76, -38.18) * mm, "end": v(677.71, -38.18) * mm});
            skLineSegment(sketch, "E106.left", {"start": v(328.76, -12.7) * mm, "end": v(328.76, -38.18) * mm});
            skLineSegment(sketch, "E106.right", {"start": v(677.71, -12.7) * mm, "end": v(677.71, -38.17) * mm});
            skSolve(sketch);
        }
        {
            var Q0;
            Q0=makeQuery(id+"F35.imprint","IMPRINT",FACE,{"disambiguationData":[TD([[makeQuery(id+"F35.imprint","IMPRINT",EDGE,{"derivedFrom":sQuery(id+"F35.wireOp",EDGE,"E106.bottom")}),1.0]])]});
            extrude(context, id + "F36", {"entities" : qUnion([Q0]), "operationType" : NewBodyOperationType.REMOVE, "oppositeDirection" : true, "depth" : 25.4 * mm});
        }
        {
            var Q0;
            Q0=makeQuery(id+"F26.opExtrude","SWEPT_FACE",FACE,{"disambiguationData":[OSD([sQuery(id+"F25.wireOp",EDGE,"E83.bottom")])]});
            var sketch = newSketch(context, id + "F37", { "sketchPlane" : qUnion([Q0])});
            skLineSegment(sketch, "E107.bottom", {"start": v(328.76, -12.7) * mm, "end": v(677.71, -12.7) * mm});
            skLineSegment(sketch, "E107.top", {"start": v(328.76, -38.18) * mm, "end": v(677.71, -38.18) * mm});
            skLineSegment(sketch, "E107.left", {"start": v(328.76, -12.7) * mm, "end": v(328.76, -38.18) * mm});
            skLineSegment(sketch, "E107.right", {"start": v(677.71, -12.7) * mm, "end": v(677.71, -38.17) * mm});
            skSolve(sketch);
        }
        {
            var Q0;
            Q0=makeQuery(id+"F37.imprint","IMPRINT",FACE,{"disambiguationData":[TD([[makeQuery(id+"F37.imprint","IMPRINT",EDGE,{"derivedFrom":sQuery(id+"F37.wireOp",EDGE,"E107.bottom")}),1.0]])]});
            extrude(context, id + "F38", {"entities" : qUnion([Q0]), "operationType" : NewBodyOperationType.REMOVE, "oppositeDirection" : true, "depth" : 25.4 * mm});
        }
        {
            var Q0;
            Q0=makeQuery(id+"F20.opExtrude","CAP_FACE",FACE,{"disambiguationData":[OSD([sQuery(id+"F19.wireOp",EDGE,"E77.bottom"),sQuery(id+"F19.wireOp",EDGE,"E77.top"),sQuery(id+"F19.wireOp",EDGE,"E77.left"),sQuery(id+"F19.wireOp",EDGE,"E77.right")])],"isStart":false});
            var sketch = newSketch(context, id + "F39", { "sketchPlane" : qUnion([Q0])});
            skLineSegment(sketch, "E108.bottom", {"start": v(262.73, 65.09) * mm, "end": v(-262.73, 65.09) * mm});
            skLineSegment(sketch, "E108.top", {"start": v(262.73, 449.26) * mm, "end": v(-262.73, 449.26) * mm});
            skLineSegment(sketch, "E108.left", {"start": v(262.73, 65.09) * mm, "end": v(262.73, 449.26) * mm});
            skLineSegment(sketch, "E108.right", {"start": v(-262.73, 65.09) * mm, "end": v(-262.73, 449.26) * mm});
            skPoint(sketch, "E108.middle", {"position": v(0, 257.18) * mm});
            skPoint(sketch, "E108.middle.positionSnap0", {"position": v(-762, 257.18) * mm});
            skPoint(sketch, "E108.middle.positionSnap1", {"position": v(0, 533.4) * mm});
            skPoint(sketch, "E108.centerSnap0", {"position": v(-762, 257.18) * mm});
            skPoint(sketch, "E108.centerSnap1", {"position": v(0, 533.4) * mm});
            skSolve(sketch);
        }
        {
            var Q0;
            Q0=makeQuery(id+"F39.imprint","IMPRINT",FACE,{"disambiguationData":[TD([[makeQuery(id+"F39.imprint","IMPRINT",EDGE,{"derivedFrom":sQuery(id+"F39.wireOp",EDGE,"E108.bottom")}),-1.0]])]});
            extrude(context, id + "F40", {"entities" : qUnion([Q0]), "depth" : 50.8 * mm});
        }
        {
            var Q0;
            Q0=makeQuery(id+"F40.opExtrude","SWEPT_EDGE",EDGE,{"disambiguationData":[OSD([sQuery(id+"F39.wireOp",EDGE,"E108.bottom"),sQuery(id+"F39.wireOp",EDGE,"E108.right")])]});
            var Q1;
            Q1=makeQuery(id+"F40.opExtrude","SWEPT_EDGE",EDGE,{"disambiguationData":[OSD([sQuery(id+"F39.wireOp",EDGE,"E108.bottom"),sQuery(id+"F39.wireOp",EDGE,"E108.left")])]});
            var Q2;
            Q2=makeQuery(id+"F40.opExtrude","SWEPT_EDGE",EDGE,{"disambiguationData":[OSD([sQuery(id+"F39.wireOp",EDGE,"E108.top"),sQuery(id+"F39.wireOp",EDGE,"E108.right")])]});
            var Q3;
            Q3=makeQuery(id+"F40.opExtrude","SWEPT_EDGE",EDGE,{"disambiguationData":[OSD([sQuery(id+"F39.wireOp",EDGE,"E108.top"),sQuery(id+"F39.wireOp",EDGE,"E108.left")])]});
            fillet(context, id + "F41", {"entities" : qUnion([Q0, Q1, Q2, Q3]), "radius" : (4 + (9 / 16)) * mm, "tangentPropagation" : true, "allowEdgeOverflow" : false});
        }
        {
            var Q0;
            Q0=makeQuery(id+"F40.opExtrude","CAP_FACE",FACE,{"disambiguationData":[OSD([sQuery(id+"F39.wireOp",EDGE,"E108.bottom"),sQuery(id+"F39.wireOp",EDGE,"E108.top"),sQuery(id+"F39.wireOp",EDGE,"E108.left"),sQuery(id+"F39.wireOp",EDGE,"E108.right")])],"isStart":false});
            shell(context, id + "F42", {"entities" : qUnion([Q0]), "thickness" : 12.7 * mm});
        }
        {
            var Q0;
            Q0=makeQuery(id+"F40.opExtrude","CAP_FACE",FACE,{"disambiguationData":[OSD([sQuery(id+"F39.wireOp",EDGE,"E108.bottom"),sQuery(id+"F39.wireOp",EDGE,"E108.top"),sQuery(id+"F39.wireOp",EDGE,"E108.left"),sQuery(id+"F39.wireOp",EDGE,"E108.right")])],"isStart":false});
            fillet(context, id + "F43", {"entities" : qUnion([Q0]), "radius" : 5.08 * mm, "tangentPropagation" : true, "allowEdgeOverflow" : false});
        }
        {
            var Q0;
            Q0=makeQuery(id+"F42.opShell","OFFSET_FACE",FACE,{"disambiguationData":[OSD([sQuery(id+"F39.wireOp",EDGE,"E108.bottom"),sQuery(id+"F39.wireOp",EDGE,"E108.top"),sQuery(id+"F39.wireOp",EDGE,"E108.left"),sQuery(id+"F39.wireOp",EDGE,"E108.right")])]});
            fillet(context, id + "F44", {"entities" : qUnion([Q0]), "radius" : 152.4 * mm, "tangentPropagation" : true, "allowEdgeOverflow" : false});
        }
        {
            var Q0;
            Q0=makeQuery(id+"F42.opShell","OFFSET_FACE",FACE,{"disambiguationData":[OSD([sQuery(id+"F39.wireOp",EDGE,"E108.bottom"),sQuery(id+"F39.wireOp",EDGE,"E108.top"),sQuery(id+"F39.wireOp",EDGE,"E108.left"),sQuery(id+"F39.wireOp",EDGE,"E108.right")])]});
            var sketch = newSketch(context, id + "F45", { "sketchPlane" : qUnion([Q0])});
            skPoint(sketch, "E109", {"position": v(0, 257.18) * mm});
            skPoint(sketch, "E109.positionSnap0", {"position": v(-152.4, 257.18) * mm});
            skPoint(sketch, "E109.positionSnap1", {"position": v(0, 338.94) * mm});
            skSolve(sketch);
        }
        {
            var Q0;
            Q0=sQuery(id+"F45.wireOp",VERTEX,"E109");
            var Q1;
            Q1=makeQuery(id+"F40.opExtrude","SWEPT_BODY",BODY,{"disambiguationData":[OSD([sQuery(id+"F39.wireOp",EDGE,"E108.bottom"),sQuery(id+"F39.wireOp",EDGE,"E108.top"),sQuery(id+"F39.wireOp",EDGE,"E108.left"),sQuery(id+"F39.wireOp",EDGE,"E108.right")])]});
            hole(context, id + "F46", {"style" : HoleStyle.C_SINK, "endStyle" : HoleEndStyle.BLIND, "holeDiameter" : 50.8 * mm, "cSinkDiameter" : 63.5 * mm, "cSinkAngle" : 82 * degree, "holeDepth" : 25.4 * mm, "isTappedThrough" : true, "tappedDepth" : 12.7 * mm, "tapClearance" : 3, "locations" : qUnion([Q0]), "scope" : qUnion([Q1])});
        }
        {
            var Q0;
            Q0=makeQuery(id+"F20.opExtrude","CAP_FACE",FACE,{"disambiguationData":[OSD([sQuery(id+"F19.wireOp",EDGE,"E77.bottom"),sQuery(id+"F19.wireOp",EDGE,"E77.top"),sQuery(id+"F19.wireOp",EDGE,"E77.left"),sQuery(id+"F19.wireOp",EDGE,"E77.right")])],"isStart":false});
            var sketch = newSketch(context, id + "F47", { "sketchPlane" : qUnion([Q0])});
            skPoint(sketch, "E110", {"position": v(0, 257.18) * mm});
            skPoint(sketch, "E110.positionSnap0", {"position": v(0, 533.4) * mm});
            skCircle(sketch, "E111", {"center": v(0, 257.18) * mm, "radius": 25.4 * mm, "construction": true});
            skSolve(sketch);
        }
        {
            var Q0;
            Q0=sQuery(id+"F47.wireOp",VERTEX,"E110");
            var Q1;
            Q1=makeQuery(id+"F1.opExtrude","SWEPT_BODY",BODY,{"disambiguationData":[OSD([sQuery(id+"F0.wireOp",EDGE,"E0.bottom"),sQuery(id+"F0.wireOp",EDGE,"E0.top"),sQuery(id+"F0.wireOp",EDGE,"E0.left"),sQuery(id+"F0.wireOp",EDGE,"E0.right")])]});
            var Q2;
            Q2=makeQuery(id+"F12.opExtrude","SWEPT_BODY",BODY,{"disambiguationData":[OSD([sQuery(id+"F6.wireOp",EDGE,"E23.bottom"),sQuery(id+"F6.wireOp",EDGE,"E23.top"),sQuery(id+"F6.wireOp",EDGE,"E23.left"),sQuery(id+"F6.wireOp",EDGE,"E23.right")])]});
            var Q3;
            Q3=makeQuery(id+"F20.opExtrude","SWEPT_BODY",BODY,{"disambiguationData":[OSD([sQuery(id+"F19.wireOp",EDGE,"E77.bottom"),sQuery(id+"F19.wireOp",EDGE,"E77.top"),sQuery(id+"F19.wireOp",EDGE,"E77.left"),sQuery(id+"F19.wireOp",EDGE,"E77.right")])]});
            hole(context, id + "F48", {"style" : HoleStyle.SIMPLE, "endStyle" : HoleEndStyle.BLIND, "holeDiameter" : 50.8 * mm, "holeDepth" : 127 * mm, "isTappedThrough" : true, "tappedDepth" : 12.7 * mm, "tapClearance" : 3, "locations" : qUnion([Q0]), "scope" : qUnion([Q1, Q2, Q3])});
        }
        {
            var Q0;
            Q0=makeQuery(id+"F14.opExtrude","SWEPT_FACE",FACE,{"disambiguationData":[OSD([sQuery(id+"F13.wireOp",EDGE,"E66.left")])]});
            var Q1;
            Q1=makeQuery(id+"F17.opExtrude","SWEPT_FACE",FACE,{"disambiguationData":[OSD([sQuery(id+"F15.wireOp",EDGE,"E73.MirrorCS")])]});
            extrude(context, id + "F49", {"entities" : qUnion([Q0]), "endBound" : BoundingType.UP_TO_SURFACE, "endBoundEntityFace" : qUnion([Q1]), "depth" : 25.4 * mm});
        }
        {
            var Q0;
            Q0=makeQuery(id+"F14.opExtrude","SWEPT_FACE",FACE,{"disambiguationData":[OSD([sQuery(id+"F13.wireOp",EDGE,"E66.right")])]});
            var Q1;
            Q1=makeQuery(id+"F18.opPattern","COPY",FACE,{"derivedFrom":makeQuery(id+"F17.opExtrude","SWEPT_FACE",FACE,{"disambiguationData":[OSD([sQuery(id+"F15.wireOp",EDGE,"E68")])]}),"instanceName":"1"});
            extrude(context, id + "F50", {"entities" : qUnion([Q0]), "endBound" : BoundingType.UP_TO_SURFACE, "endBoundEntityFace" : qUnion([Q1]), "depth" : 25.4 * mm});
        }
        {
            var Q0;
            Q0=makeQuery(id+"F49.opExtrude","SWEPT_BODY",BODY,{"disambiguationData":[OSD([sQuery(id+"F13.wireOp",EDGE,"E66.left")])]});
            var Q1;
            Q1=makeQuery(id+"F14.opExtrude","SWEPT_BODY",BODY,{"disambiguationData":[OSD([sQuery(id+"F13.wireOp",EDGE,"E66.bottom"),sQuery(id+"F13.wireOp",EDGE,"E66.top"),sQuery(id+"F13.wireOp",EDGE,"E66.left"),sQuery(id+"F13.wireOp",EDGE,"E66.right"),sQuery(id+"F13.wireOp",EDGE,"E67.bottom"),sQuery(id+"F13.wireOp",EDGE,"E67.top"),sQuery(id+"F13.wireOp",EDGE,"E67.left"),sQuery(id+"F13.wireOp",EDGE,"E67.right")])]});
            var Q2;
            Q2=makeQuery(id+"F50.opExtrude","SWEPT_BODY",BODY,{"disambiguationData":[OSD([sQuery(id+"F13.wireOp",EDGE,"E66.right")])]});
            booleanBodies(context, id + "F51", {"operationType" : BooleanOperationType.UNION, "tools" : qUnion([Q0, Q1, Q2])});
        }
        {
            var Q0;
            Q0=makeQuery(id+"F14.opExtrude","CAP_FACE",FACE,{"disambiguationData":[OSD([sQuery(id+"F13.wireOp",EDGE,"E66.bottom"),sQuery(id+"F13.wireOp",EDGE,"E66.top"),sQuery(id+"F13.wireOp",EDGE,"E66.left"),sQuery(id+"F13.wireOp",EDGE,"E66.right"),sQuery(id+"F13.wireOp",EDGE,"E67.bottom"),sQuery(id+"F13.wireOp",EDGE,"E67.top"),sQuery(id+"F13.wireOp",EDGE,"E67.left"),sQuery(id+"F13.wireOp",EDGE,"E67.right")])],"isStart":true});
            var sketch = newSketch(context, id + "F52", { "sketchPlane" : qUnion([Q0])});
            skLineSegment(sketch, "E112", {"start": v(-667.12, 50.8) * mm, "end": v(667.12, 50.8) * mm});
            skLineSegment(sketch, "E113", {"start": v(-667.12, 50.8) * mm, "end": v(-667.12, 76.2) * mm});
            skLineSegment(sketch, "E114", {"start": v(-667.12, 76.2) * mm, "end": v(667.12, 76.2) * mm});
            skLineSegment(sketch, "E115", {"start": v(667.12, 76.2) * mm, "end": v(667.12, 50.8) * mm});
            skLineSegment(sketch, "E116", {"start": v(-609.6, 266.7) * mm, "end": v(609.6, 266.7) * mm, "construction": true});
            skLineSegment(sketch, "E117.MirrorCS", {"start": v(-667.12, 482.6) * mm, "end": v(-667.12, 457.2) * mm});
            skLineSegment(sketch, "E118.MirrorCS", {"start": v(667.12, 457.2) * mm, "end": v(667.12, 482.6) * mm});
            skLineSegment(sketch, "E119.MirrorCS", {"start": v(-667.12, 482.6) * mm, "end": v(667.12, 482.6) * mm});
            skLineSegment(sketch, "E120.MirrorCS", {"start": v(-667.12, 457.2) * mm, "end": v(667.12, 457.2) * mm});
            skSolve(sketch);
        }
        {
            var Q0;
            {var subQ0=sQuery(id+"F52.wireOp",EDGE,"E119.MirrorCS");var subQ1=sQuery(id+"F13.wireOp",EDGE,"E66.left");var subQ2=makeQuery(id+"F14.opExtrude","CAP_EDGE",EDGE,{"disambiguationData":[OSD([subQ1])],"isStart":true});var subQ3=makeQuery(id+"F51.opBoolean","MERGE",EDGE,{"derivedFrom":[subQ2,makeQuery(id+"F49.opExtrude","CAP_EDGE",EDGE,{"disambiguationData":[OSD([subQ1]),TDD([subQ2])],"isStart":false})]});var subQ4=makeQuery(id+"F52.imprint","INTERSECT",VERTEX,{"derivedFrom":[subQ3,subQ0]});var subQ5=sQuery(id+"F13.wireOp",EDGE,"E66.right");var subQ6=makeQuery(id+"F51.opBoolean","MERGE",EDGE,{"derivedFrom":[makeQuery(id+"F14.opExtrude","CAP_EDGE",EDGE,{"disambiguationData":[OSD([subQ5])],"isStart":true}),makeQuery(id+"F50.opExtrude","TWEAK_EDGE",EDGE,{"derivedFrom":[makeQuery(id+"F14.opExtrude","SWEPT_FACE",FACE,{"disambiguationData":[OSD([subQ5])]}),makeQuery(id+"F18.opPattern","COPY",FACE,{"derivedFrom":makeQuery(id+"F17.opExtrude","SWEPT_FACE",FACE,{"disambiguationData":[OSD([sQuery(id+"F15.wireOp",EDGE,"E68")])]}),"instanceName":"1"})]})]});var subQ7=makeQuery(id+"F52.imprint","INTERSECT",VERTEX,{"derivedFrom":[subQ6,subQ0]});Q0=makeQuery(id+"F52.imprint","IMPRINT",FACE,{"disambiguationData":[TD([[makeQuery(id+"F52.imprint","IMPRINT",EDGE,{"disambiguationData":[TD([[subQ4,-1.0],[subQ7,1.0]])],"derivedFrom":subQ0}),1.0]])]});}
            var Q1;
            {var subQ0=sQuery(id+"F52.wireOp",EDGE,"E117.MirrorCS");Q1=makeQuery(id+"F52.imprint","IMPRINT",FACE,{"disambiguationData":[TD([[makeQuery(id+"F52.imprint","IMPRINT",EDGE,{"derivedFrom":subQ0}),1.0]])]});}
            var Q2;
            {var subQ0=sQuery(id+"F52.wireOp",EDGE,"E118.MirrorCS");Q2=makeQuery(id+"F52.imprint","IMPRINT",FACE,{"disambiguationData":[TD([[makeQuery(id+"F52.imprint","IMPRINT",EDGE,{"derivedFrom":subQ0}),1.0]])]});}
            var Q3;
            {var subQ4=sQuery(id+"F52.wireOp",EDGE,"E115");Q3=makeQuery(id+"F52.imprint","IMPRINT",FACE,{"disambiguationData":[TD([[makeQuery(id+"F52.imprint","IMPRINT",EDGE,{"derivedFrom":subQ4}),-1.0]])]});}
            var Q4;
            {var subQ0=sQuery(id+"F52.wireOp",EDGE,"E112");var subQ1=sQuery(id+"F13.wireOp",EDGE,"E66.left");var subQ2=makeQuery(id+"F14.opExtrude","CAP_EDGE",EDGE,{"disambiguationData":[OSD([subQ1])],"isStart":true});var subQ3=makeQuery(id+"F51.opBoolean","MERGE",EDGE,{"derivedFrom":[subQ2,makeQuery(id+"F49.opExtrude","CAP_EDGE",EDGE,{"disambiguationData":[OSD([subQ1]),TDD([subQ2])],"isStart":false})]});var subQ4=makeQuery(id+"F52.imprint","INTERSECT",VERTEX,{"derivedFrom":[subQ3,subQ0]});var subQ5=sQuery(id+"F13.wireOp",EDGE,"E66.right");var subQ6=makeQuery(id+"F51.opBoolean","MERGE",EDGE,{"derivedFrom":[makeQuery(id+"F14.opExtrude","CAP_EDGE",EDGE,{"disambiguationData":[OSD([subQ5])],"isStart":true}),makeQuery(id+"F50.opExtrude","TWEAK_EDGE",EDGE,{"derivedFrom":[makeQuery(id+"F14.opExtrude","SWEPT_FACE",FACE,{"disambiguationData":[OSD([subQ5])]}),makeQuery(id+"F18.opPattern","COPY",FACE,{"derivedFrom":makeQuery(id+"F17.opExtrude","SWEPT_FACE",FACE,{"disambiguationData":[OSD([sQuery(id+"F15.wireOp",EDGE,"E68")])]}),"instanceName":"1"})]})]});var subQ7=makeQuery(id+"F52.imprint","INTERSECT",VERTEX,{"derivedFrom":[subQ6,subQ0]});Q4=makeQuery(id+"F52.imprint","IMPRINT",FACE,{"disambiguationData":[TD([[makeQuery(id+"F52.imprint","IMPRINT",EDGE,{"disambiguationData":[TD([[subQ4,-1.0],[subQ7,1.0]])],"derivedFrom":subQ0}),-1.0]])]});}
            var Q5;
            {var subQ4=sQuery(id+"F52.wireOp",EDGE,"E113");Q5=makeQuery(id+"F52.imprint","IMPRINT",FACE,{"disambiguationData":[TD([[makeQuery(id+"F52.imprint","IMPRINT",EDGE,{"derivedFrom":subQ4}),-1.0]])]});}
            extrude(context, id + "F53", {"entities" : qUnion([Q0, Q1, Q2, Q3, Q4, Q5]), "operationType" : NewBodyOperationType.REMOVE, "oppositeDirection" : true, "depth" : 50.8 * mm});
        }
        {
            var Q0;
            Q0=makeQuery(id+"F12.opExtrude","CAP_FACE",FACE,{"disambiguationData":[OSD([sQuery(id+"F6.wireOp",EDGE,"E23.bottom"),sQuery(id+"F6.wireOp",EDGE,"E23.top"),sQuery(id+"F6.wireOp",EDGE,"E23.left"),sQuery(id+"F6.wireOp",EDGE,"E23.right")])],"isStart":false});
            var sketch = newSketch(context, id + "F54", { "sketchPlane" : qUnion([Q0])});
            skLineSegment(sketch, "E121.bottom", {"start": v(243.68, -310.36) * mm, "end": v(-243.68, -310.36) * mm});
            skLineSegment(sketch, "E121.top", {"start": v(243.68, -172.24) * mm, "end": v(-243.68, -172.24) * mm});
            skLineSegment(sketch, "E121.left", {"start": v(243.68, -310.36) * mm, "end": v(243.68, -172.24) * mm});
            skLineSegment(sketch, "E121.right", {"start": v(-243.68, -310.36) * mm, "end": v(-243.68, -172.24) * mm});
            skPoint(sketch, "E121.middle", {"position": v(0, -241.3) * mm});
            skSolve(sketch);
        }
        {
            var Q0;
            Q0=makeQuery(id+"F54.imprint","IMPRINT",FACE,{"disambiguationData":[TD([[makeQuery(id+"F54.imprint","IMPRINT",EDGE,{"derivedFrom":sQuery(id+"F54.wireOp",EDGE,"E121.bottom")}),-1.0]])]});
            extrude(context, id + "F55", {"entities" : qUnion([Q0]), "oppositeDirection" : true, "depth" : 12.7 * mm});
        }
        {
            var Q0;
            Q0=makeQuery(id+"F55.opExtrude","CAP_FACE",FACE,{"disambiguationData":[OSD([sQuery(id+"F54.wireOp",EDGE,"E121.bottom"),sQuery(id+"F54.wireOp",EDGE,"E121.top"),sQuery(id+"F54.wireOp",EDGE,"E121.left"),sQuery(id+"F54.wireOp",EDGE,"E121.right")])],"isStart":true});
            var sketch = newSketch(context, id + "F56", { "sketchPlane" : qUnion([Q0])});
            skLineSegment(sketch, "E122.bottom", {"start": v(82.55, -172.24) * mm, "end": v(-82.55, -172.24) * mm});
            skLineSegment(sketch, "E122.top", {"start": v(82.55, -197.64) * mm, "end": v(-82.55, -197.64) * mm});
            skLineSegment(sketch, "E122.left", {"start": v(82.55, -172.24) * mm, "end": v(82.55, -197.64) * mm});
            skLineSegment(sketch, "E122.right", {"start": v(-82.55, -172.24) * mm, "end": v(-82.55, -197.64) * mm});
            skPoint(sketch, "E122.middle", {"position": v(0, -184.94) * mm});
            skLineSegment(sketch, "E123", {"start": v(-82.55, -172.24) * mm, "end": v(-60.33, -197.64) * mm});
            skLineSegment(sketch, "E124", {"start": v(82.55, -172.24) * mm, "end": v(60.33, -197.64) * mm});
            skSolve(sketch);
        }
        {
            var Q0;
            Q0=makeQuery(id+"F56.imprint","IMPRINT",FACE,{"disambiguationData":[TD([[makeQuery(id+"F56.imprint","IMPRINT",EDGE,{"derivedFrom":sQuery(id+"F56.wireOp",EDGE,"E122.bottom")}),1.0]])]});
            extrude(context, id + "F57", {"entities" : qUnion([Q0]), "operationType" : NewBodyOperationType.REMOVE, "oppositeDirection" : true, "depth" : 25.4 * mm});
        }
        {
            var Q0;
            Q0=makeQuery(id+"F57.boolean.opBoolean","COPY",EDGE,{"derivedFrom":makeQuery(id+"F57.opExtrude","SWEPT_EDGE",EDGE,{"disambiguationData":[OSD([sQuery(id+"F56.wireOp",EDGE,"E122.top"),sQuery(id+"F56.wireOp",EDGE,"E124")])]})});
            var Q1;
            Q1=makeQuery(id+"F57.boolean.opBoolean","COPY",EDGE,{"derivedFrom":makeQuery(id+"F57.opExtrude","SWEPT_EDGE",EDGE,{"disambiguationData":[OSD([sQuery(id+"F56.wireOp",EDGE,"E122.top"),sQuery(id+"F56.wireOp",EDGE,"E123")])]})});
            fillet(context, id + "F58", {"entities" : qUnion([Q0, Q1]), "radius" : 25.4 * mm, "tangentPropagation" : true, "allowEdgeOverflow" : false});
        }
        {
            var Q0;
            Q0=makeQuery(id+"F3.boolean.opBoolean","COPY",FACE,{"derivedFrom":makeQuery(id+"F3.opExtrude","CAP_FACE",FACE,{"disambiguationData":[OSD([sQuery(id+"F2.wireOp",EDGE,"E1.bottom"),sQuery(id+"F2.wireOp",EDGE,"E1.top"),sQuery(id+"F2.wireOp",EDGE,"E1.left"),sQuery(id+"F2.wireOp",EDGE,"E1.right")])],"isStart":false})});
            var sketch = newSketch(context, id + "F59", { "sketchPlane" : qUnion([Q0])});
            skPoint(sketch, "E125.positionSnap0", {"position": v(0, 311.15) * mm});
            skLineSegment(sketch, "E126.bottom", {"start": v(-168.28, 234.95) * mm, "end": v(168.28, 234.95) * mm});
            skLineSegment(sketch, "E126.top", {"start": v(-168.28, -76.2) * mm, "end": v(168.28, -76.2) * mm});
            skLineSegment(sketch, "E126.left", {"start": v(-168.28, 234.95) * mm, "end": v(-168.28, -76.2) * mm});
            skLineSegment(sketch, "E126.right", {"start": v(168.28, 234.95) * mm, "end": v(168.28, -76.2) * mm});
            skPoint(sketch, "E126.middle", {"position": v(0, 79.38) * mm});
            skSolve(sketch);
        }
        {
            var Q0;
            Q0 = qSketchRegion(id + "F59", true);
            extrude(context, id + "F60", {"entities" : qUnion([Q0]), "operationType" : NewBodyOperationType.REMOVE, "oppositeDirection" : true, "depth" : 50.8 * mm});
        }
    });
